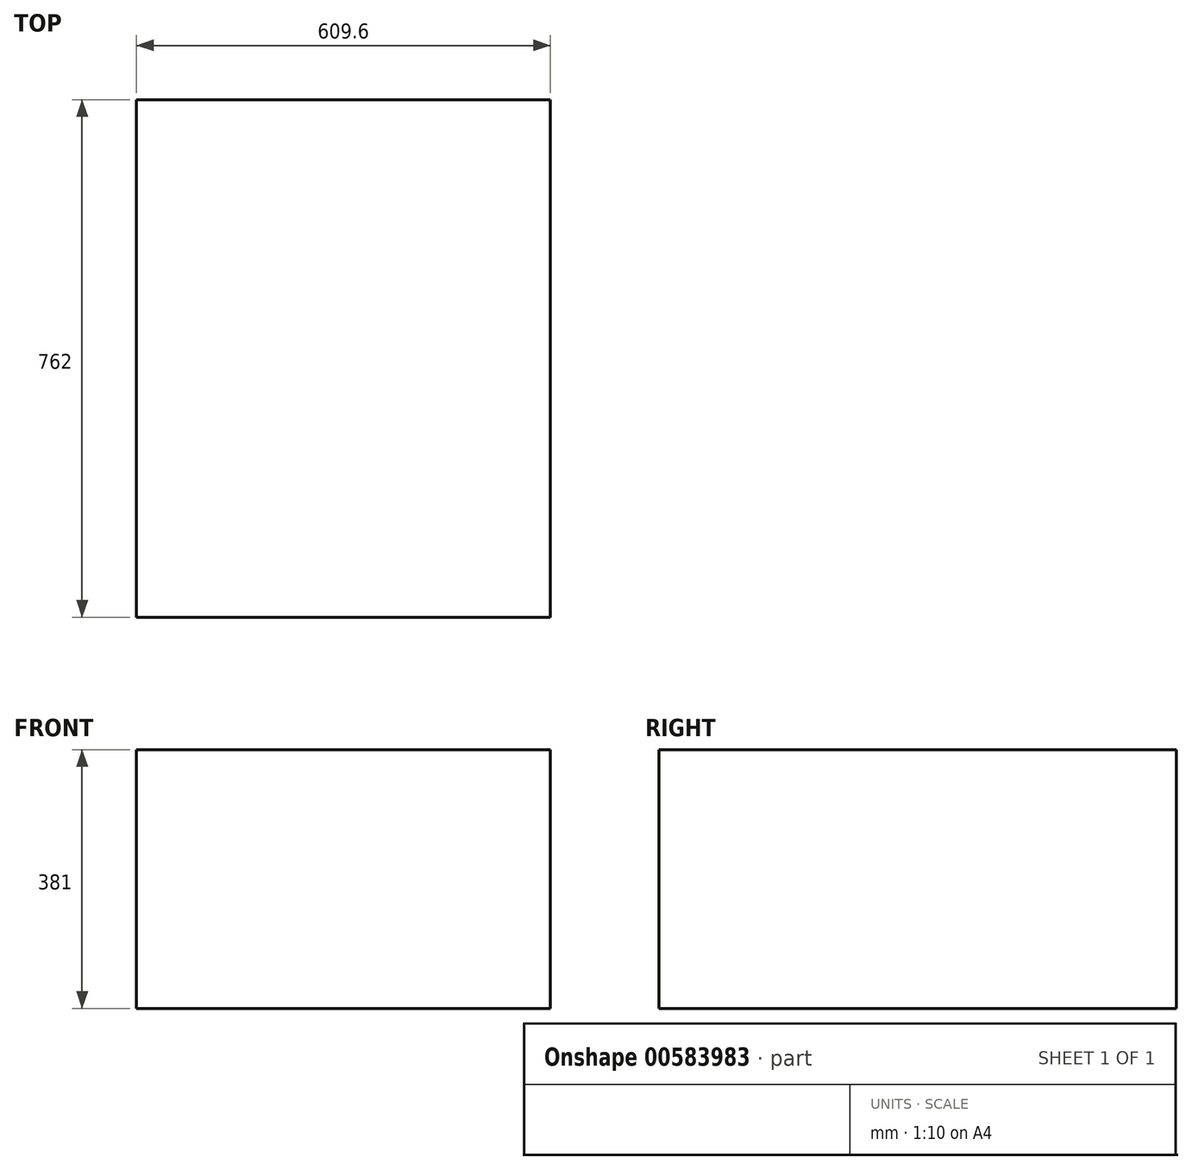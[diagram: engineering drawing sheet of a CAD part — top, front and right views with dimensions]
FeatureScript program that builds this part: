
annotation { "Feature Type Name" : "Feature", "Feature Type Description" : "" }
export const myFeature = defineFeature(function(context is Context, id is Id, definition is map)
    precondition{}
    {
        {
            var Q0;
            Q0=qCreatedBy(makeId("Top.planeOp"),FACE);
            var sketch = newSketch(context, id + "F0", { "sketchPlane" : qUnion([Q0])});
            skLineSegment(sketch, "E0.bottom", {"start": v(-300.23, 519.43) * mm, "end": v(309.37, 519.43) * mm});
            skLineSegment(sketch, "E0.top", {"start": v(-300.23, -242.57) * mm, "end": v(309.37, -242.57) * mm});
            skLineSegment(sketch, "E0.left", {"start": v(-300.23, 519.43) * mm, "end": v(-300.23, -242.57) * mm});
            skLineSegment(sketch, "E0.right", {"start": v(309.37, 519.43) * mm, "end": v(309.37, -242.57) * mm});
            skSolve(sketch);
        }
        {
            var Q0;
            Q0=makeQuery(id+"F0.imprint","IMPRINT",FACE,{"disambiguationData":[TD([[makeQuery(id+"F0.imprint","IMPRINT",EDGE,{"derivedFrom":sQuery(id+"F0.wireOp",EDGE,"E0.bottom")}),-1.0]])]});
            extrude(context, id + "F1", {"entities" : qUnion([Q0]), "depth" : 381 * mm, "offsetDistance" : 25.4 * mm});
        }
    });
